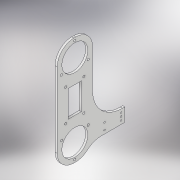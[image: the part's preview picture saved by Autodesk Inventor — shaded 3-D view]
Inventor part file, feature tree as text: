
AUTODESK INVENTOR PART (.ipt)
format: ipt  version: 2019 (Build 230136000, 136)  size: 238,080 bytes
history: native  units: in
note: dims shown in document units (in); Inventor stores cm internally (conversion verified against a paired STEP export)
features: sketch x19, hole x16, extrude x4
ambient origin geometry x8: Origin, YZ Plane, XZ Plane, XY Plane, X Axis, Y Axis, Z Axis, Center Point
bodies: Solid1 (feature_tree)
feature tree (39):
  hole  "Hole1"  [1 undecoded]
  hole  "Hole2"  [1 undecoded]
  hole  "Hole3"  [1 undecoded]
  hole  "Hole4"  [1 undecoded]
  hole  "Hole5"  [1 undecoded]
  hole  "Hole6"  [1 undecoded]
  hole  "Hole7"  [1 undecoded]
  hole  "Hole8"  [1 undecoded]
  hole  "Hole9"  [1 undecoded]
  hole  "Hole10"  [1 undecoded]
  hole  "Hole11"  [1 undecoded]
  hole  "Hole12"  [1 undecoded]
  extrude  "Extrusion1"  [1 undecoded]
  hole  "Hole13"  [1 undecoded]
  extrude  "Extrusion2"  [1 undecoded]
  hole  "Hole14"  [1 undecoded]
  extrude  "Extrusion3"  [1 undecoded]
  hole  "Hole15"  [1 undecoded]
  extrude  "Extrusion4"  [1 undecoded]
  sketch  "Sketch1"  dims[d0=0.266in d1=0.2362in d2=0.507in d3=0.0787in d4=0.563in d5=0.5883in d6=0.8108in]
  sketch  "Sketch2"  dims[d7=0.266in d8=0.2362in d9=0.507in d10=0.0787in d11=0.563in d12=0.5883in d13=0.8108in]
  sketch  "Sketch3"  dims[d14=0.266in d15=0.2362in d16=0.507in d17=0.0787in d18=0.563in d19=0.5883in d20=0.8108in]
  sketch  "Sketch4"  dims[d21=0.266in d22=0.2362in d23=0.507in d24=0.0787in d25=0.563in d26=0.5883in d27=0.8108in]
  sketch  "Sketch5"  dims[d28=0.266in d29=0.2362in d30=0.507in d31=0.0787in d32=0.563in d33=0.5883in d34=0.8108in]
  sketch  "Sketch6"  dims[d35=0.266in d36=0.2362in d37=0.507in d38=0.0787in d39=0.563in d40=0.5883in d41=0.8108in]
  sketch  "Sketch7"  dims[d42=0.266in d43=0.2362in d44=0.507in d45=0.0787in d46=0.563in d47=0.5883in d48=0.8108in]
  sketch  "Sketch8"  dims[d49=0.266in d50=0.2362in d51=0.507in d52=0.0787in d53=0.563in d54=0.5883in d55=0.8108in]
  sketch  "Sketch9"  dims[d56=0.266in d57=0.2362in d58=0.507in d59=0.0787in d60=0.563in d61=0.5883in d62=0.8108in]
  sketch  "Sketch10"  dims[d63=0.266in d64=0.2362in d65=0.507in d66=0.0787in d67=0.563in d68=0.5883in d69=0.8108in]
  sketch  "Sketch11"  dims[d70=0.177in d71=0.2362in d72=0.332in d73=0.0787in d74=0.563in d75=0.5883in d76=0.8108in]
  sketch  "Sketch12"  dims[d77=0.177in d78=0.2362in d79=0.332in d80=0.0787in d81=0.563in d82=0.5883in d83=0.8108in d84=0.3937in d85=0.0in]
  sketch  "Sketch13"  dims[d86=3.0709in d87=0.2362in d88=0.332in d89=0.0787in d90=0.563in d91=3.0709in d92=0.8108in d93=0.3937in d94=0.0in]
  sketch  "Sketch14"  dims[d95=3.0709in d96=0.2362in d97=0.332in d98=0.0787in d99=0.563in d100=3.0709in d101=0.8108in d102=0.3937in d103=0.0in]
  sketch  "Sketch15"  dims[d104=0.201in d105=0.2362in d106=0.385in d107=0.0787in d108=0.563in d109=3.0709in d110=0.8108in d111=0.1437in d112=0.0in]
  sketch  "Sketch16"
  sketch  "Sketch17"
  sketch  "Sketch18"
  sketch  "Sketch19"
  hole  "hole_plate1"  [1 undecoded]
note: 20 required parameter values undecoded (feature->parameter linkage not recoverable at this tier; creation-order binding heuristic only, values carry confidence <= 0.55)
